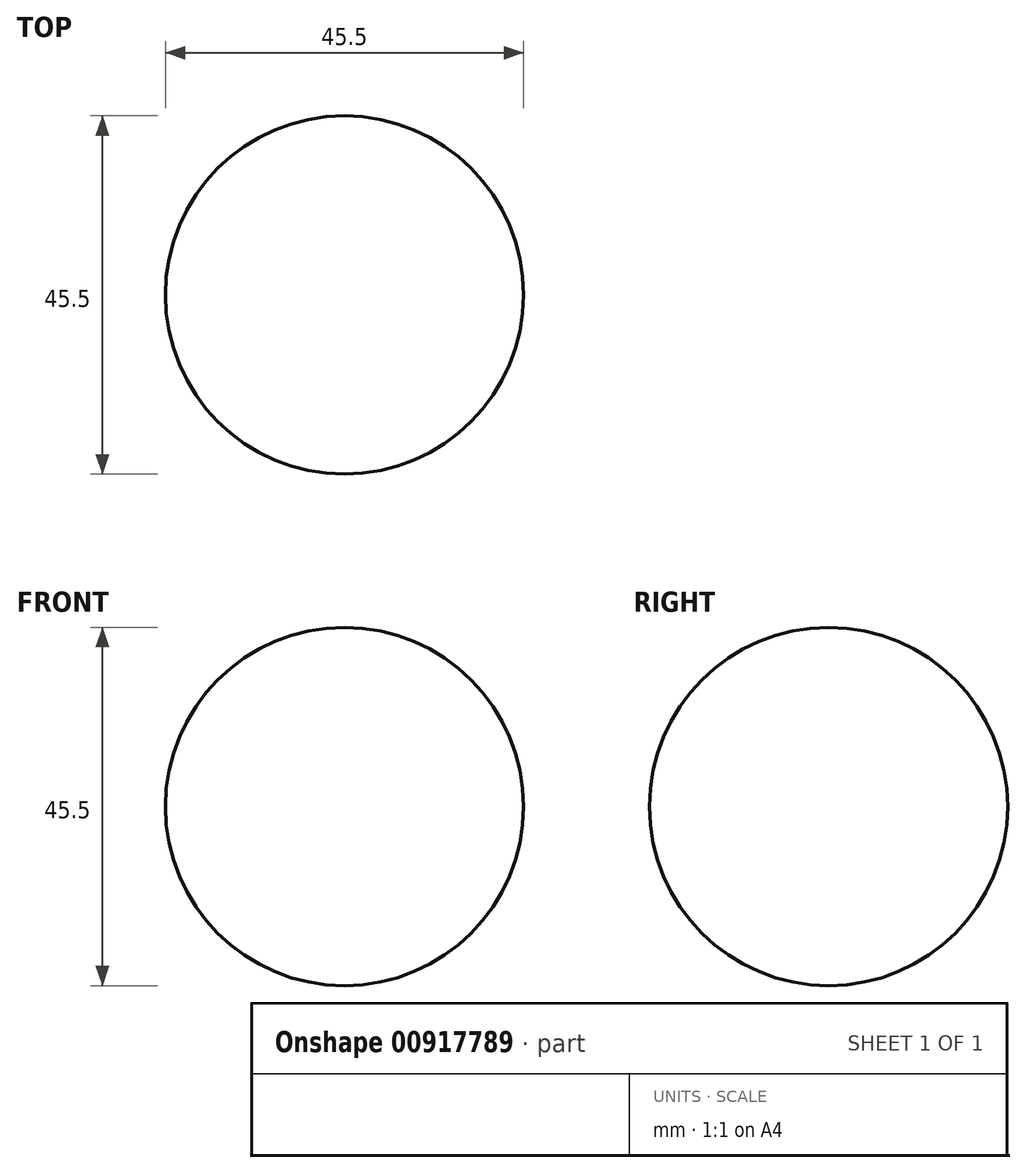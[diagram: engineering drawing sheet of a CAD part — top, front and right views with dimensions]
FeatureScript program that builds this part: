
annotation { "Feature Type Name" : "Feature", "Feature Type Description" : "" }
export const myFeature = defineFeature(function(context is Context, id is Id, definition is map)
    precondition{}
    {
        {
            var Q0;
            Q0=qCreatedBy(makeId("Front.planeOp"),FACE);
            var sketch = newSketch(context, id + "F0", { "sketchPlane" : qUnion([Q0])});
            skArc(sketch, "E0", {"start": v(0, -22.75) * mm, "mid": v(22.75, 0) * mm, "end": v(0, 22.75) * mm});
            skLineSegment(sketch, "E1", {"start": v(0, 22.75) * mm, "end": v(0, -22.75) * mm});
            skSolve(sketch);
        }
        {
            var Q0;
            Q0=makeQuery(id+"F0.imprint","IMPRINT",FACE,{"disambiguationData":[TD([[makeQuery(id+"F0.imprint","IMPRINT",EDGE,{"derivedFrom":sQuery(id+"F0.wireOp",EDGE,"E0")}),1.0]])]});
            var Q1;
            Q1=sQuery(id+"F0.wireOp",EDGE,"E1");
            revolve(context, id + "F1", {"surfaceOperationType" : NewSurfaceOperationType.NEW, "entities" : qUnion([Q0]), "axis" : qUnion([Q1]), "revolveType" : RevolveType.FULL});
        }
    });
